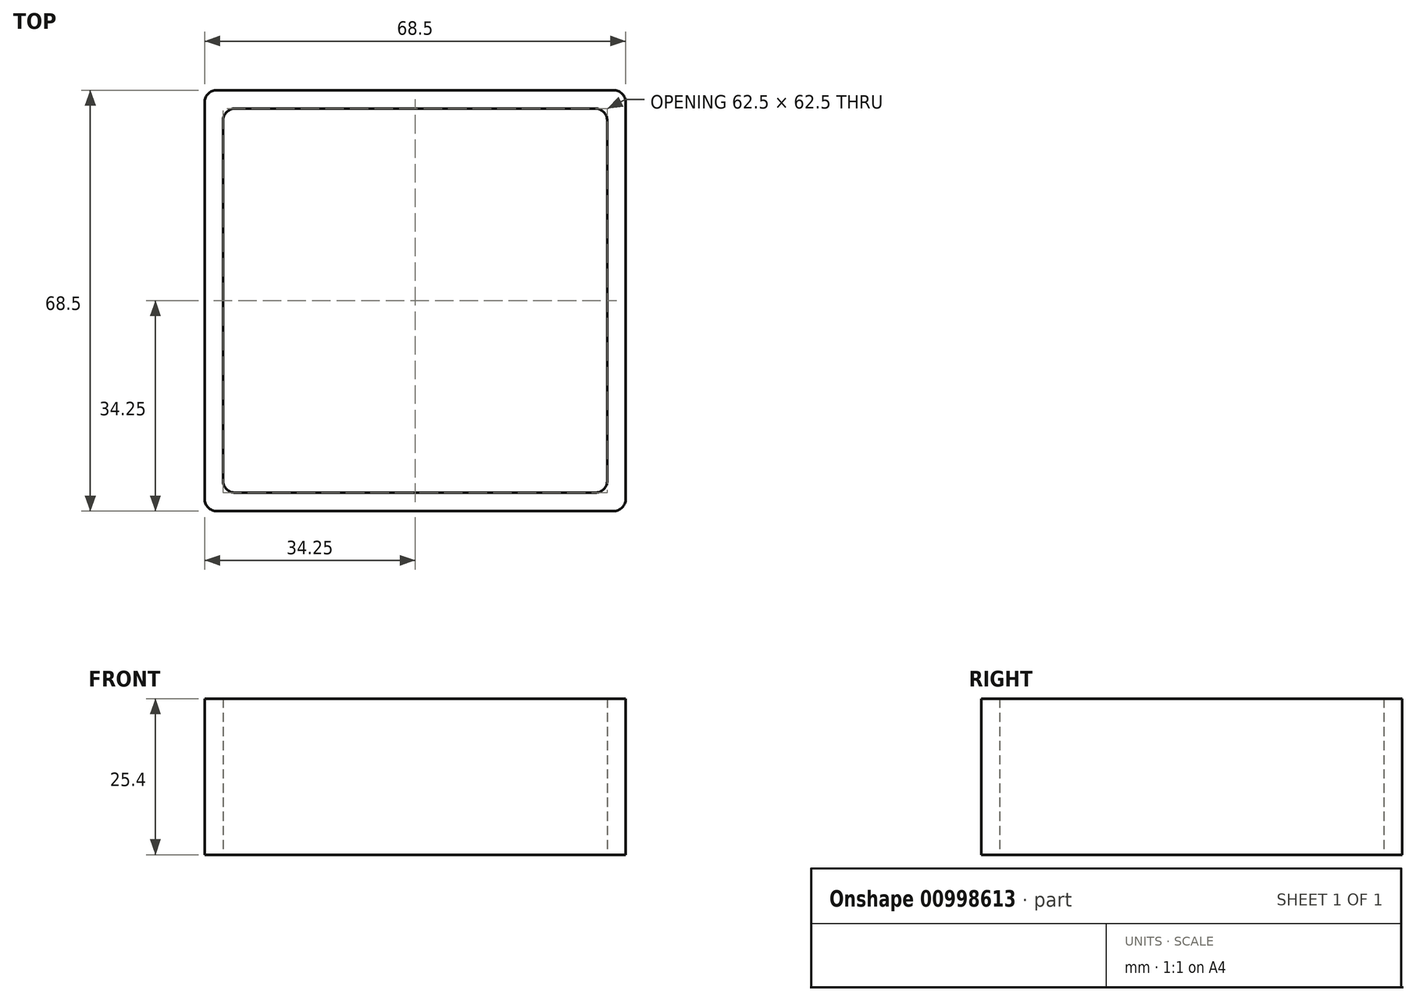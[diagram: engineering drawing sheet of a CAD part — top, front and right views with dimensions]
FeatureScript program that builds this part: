
annotation { "Feature Type Name" : "Feature", "Feature Type Description" : "" }
export const myFeature = defineFeature(function(context is Context, id is Id, definition is map)
    precondition{}
    {
        {
            var Q0;
            Q0=qCreatedBy(makeId("Top.planeOp"),FACE);
            var sketch = newSketch(context, id + "F0", { "sketchPlane" : qUnion([Q0])});
            skLineSegment(sketch, "E0.bottom", {"start": v(31.25, -31.25) * mm, "end": v(-31.25, -31.25) * mm});
            skLineSegment(sketch, "E0.top", {"start": v(31.25, 31.25) * mm, "end": v(-31.25, 31.25) * mm});
            skLineSegment(sketch, "E0.left", {"start": v(31.25, -31.25) * mm, "end": v(31.25, 31.25) * mm});
            skLineSegment(sketch, "E0.right", {"start": v(-31.25, -31.25) * mm, "end": v(-31.25, 31.25) * mm});
            skPoint(sketch, "E0.middle", {"position": v(0, 0) * mm});
            skLineSegment(sketch, "E1.bottom", {"start": v(-34.25, -34.25) * mm, "end": v(34.25, -34.25) * mm});
            skLineSegment(sketch, "E1.top", {"start": v(-34.25, 34.25) * mm, "end": v(34.25, 34.25) * mm});
            skLineSegment(sketch, "E1.left", {"start": v(-34.25, -34.25) * mm, "end": v(-34.25, 34.25) * mm});
            skLineSegment(sketch, "E1.right", {"start": v(34.25, -34.25) * mm, "end": v(34.25, 34.25) * mm});
            skSolve(sketch);
        }
        {
            var Q0;
            Q0 = qSketchRegion(id + "F0", true);
            extrude(context, id + "F1", {"entities" : qUnion([Q0]), "depth" : 25.4 * mm, "offsetDistance" : 25 * mm});
        }
        {
            var Q0;
            Q0=makeQuery(id+"F1.opExtrude","SWEPT_EDGE",EDGE,{"disambiguationData":[OSD([sQuery(id+"F0.wireOp",EDGE,"E0.top"),sQuery(id+"F0.wireOp",EDGE,"E0.left")])]});
            var Q1;
            Q1=makeQuery(id+"F1.opExtrude","SWEPT_EDGE",EDGE,{"disambiguationData":[OSD([sQuery(id+"F0.wireOp",EDGE,"E0.top"),sQuery(id+"F0.wireOp",EDGE,"E0.right")])]});
            var Q2;
            Q2=makeQuery(id+"F1.opExtrude","SWEPT_EDGE",EDGE,{"disambiguationData":[OSD([sQuery(id+"F0.wireOp",EDGE,"E0.bottom"),sQuery(id+"F0.wireOp",EDGE,"E0.right")])]});
            var Q3;
            Q3=makeQuery(id+"F1.opExtrude","SWEPT_EDGE",EDGE,{"disambiguationData":[OSD([sQuery(id+"F0.wireOp",EDGE,"E0.bottom"),sQuery(id+"F0.wireOp",EDGE,"E0.left")])]});
            var Q4;
            Q4=makeQuery(id+"F1.opExtrude","SWEPT_EDGE",EDGE,{"disambiguationData":[OSD([sQuery(id+"F0.wireOp",EDGE,"E1.top"),sQuery(id+"F0.wireOp",EDGE,"E1.left")])]});
            var Q5;
            Q5=makeQuery(id+"F1.opExtrude","SWEPT_EDGE",EDGE,{"disambiguationData":[OSD([sQuery(id+"F0.wireOp",EDGE,"E1.top"),sQuery(id+"F0.wireOp",EDGE,"E1.right")])]});
            var Q6;
            Q6=makeQuery(id+"F1.opExtrude","SWEPT_EDGE",EDGE,{"disambiguationData":[OSD([sQuery(id+"F0.wireOp",EDGE,"E1.bottom"),sQuery(id+"F0.wireOp",EDGE,"E1.left")])]});
            var Q7;
            Q7=makeQuery(id+"F1.opExtrude","SWEPT_EDGE",EDGE,{"disambiguationData":[OSD([sQuery(id+"F0.wireOp",EDGE,"E1.bottom"),sQuery(id+"F0.wireOp",EDGE,"E1.right")])]});
            fillet(context, id + "F2", {"entities" : qUnion([Q0, Q1, Q2, Q3, Q4, Q5, Q6, Q7]), "radius" : 2 * mm, "tangentPropagation" : true, "allowEdgeOverflow" : false});
        }
    });
